# Revit family: Guide_Rail_System-Zoeller-(Z-Rail_Assembly)
name_source: partatom
category: Mechanical Equipment
revit_build: Autodesk Revit 2014 (Build: 20130308_1515(x64)
units: mm (PartAtom-declared; Revit-internal decimal feet)

## types (20) — shared parameters
Assembly Code = D2030400
Bracket Height = 60"
CW Connection = Yes
Default Elevation = 60"
Description = Z-Rail Assembly
HW Connection = No
Height = 60"
Length = 8 1/2"
Manufacturer = Zoeller
Price = Prices may vary. Please consult Manufacturer Representative for most up-to-date price list.
Product Documentation Link = https://www.zoellerpumps.com
Product Page URL = https://www.zoellerpumps.com
Revised Date = 04/10/2019
URL = http://www.zoellerpumps.com
Vent Connection = No
Waste Connection = Yes
Width = 6 3/4"

## per-type parameters (varying)
| type | Carrier Void Diameter 1 | Carrier Void Diameter 2 | Carrier Void Diameter 3 | Elbow Outer Diameter | Material | Model | Non-Sparking Brass | Pump Discharge Diameter | Pump Discharge Radius | Rail Discharge Outer Diameter | Rail Plate Material | Rail System Discharge Diameter | Rail System Discharge Radius | Upper Rail Support Bracket |
| 39-0134 1-1/4" Z-Rail | 1 17/32" | 1 25/32" | 1 31/32" | 1 3/4" | Metal-Zoeller-Epoxy Powder Coated Ductile Iron | 39-0134 | No | 1 1/4" | 5/8" | 2 3/8" | Metal-Zoeller-Powder Coated Ductile Iron | 2" | 1" | Support_Bracket-Upper-Zoeller-Rail_Sytem-152383 : 15-2383 |
| 39-0131 1-1/2" Z-Rail | 1 17/32" | 1 25/32" | 1 31/32" | 2" | Metal-Zoeller-Epoxy Powder Coated Ductile Iron | 39-0131 | No | 1 1/2" | 3/4" | 2 3/8" | Metal-Zoeller-Powder Coated Ductile Iron | 2" | 1" | Support_Bracket-Upper-Zoeller-Rail_Sytem-152383 : 15-2383 |
| 39-0128 2" Z-Rail | 2 1/32" | 2 9/32" | 2 15/32" | 2 1/2" | Metal-Zoeller-Epoxy Powder Coated Ductile Iron | 39-0128 | No | 2" | 1" | 2 3/8" | Metal-Zoeller-Powder Coated Ductile Iron | 2" | 1" | Support_Bracket-Upper-Zoeller-Rail_Sytem-152383 : 15-2383 |
| 39-0135 1-1/4" Z-Rail | 1 17/32" | 1 25/32" | 1 31/32" | 1 3/4" | Metal-Zoeller-Epoxy Powder Coated Ductile Iron | 39-0135 | No | 1 1/4" | 5/8" | 2 3/8" | Metal-Zoeller-Powder Coated Ductile Iron | 2" | 1" | Support_Bracket-Upper-Zoeller-Rail_Sytem-152383 : 15-2383 SS |
| 39-0136 1-1/4" Z-Rail | 1 17/32" | 1 25/32" | 1 31/32" | 1 3/4" | Metal-Zoeller-Powder Coated Ductile Iron | 39-0136 | Yes | 1 1/4" | 5/8" | 2 3/8" | Metal-Zoeller-Bronze | 2" | 1" | Support_Bracket-Upper-Zoeller-Rail_Sytem-152383 : 15-2383 |
| 39-0143 1-1/4" Z-Rail | 1 17/32" | 1 25/32" | 1 31/32" | 1 3/4" | Metal-Zoeller-Powder Coated Ductile Iron | 39-0143 | Yes | 1 1/4" | 5/8" | 2 3/8" | Metal-Zoeller-Bronze | 2" | 1" | Support_Bracket-Upper-Zoeller-Rail_Sytem-152383 : 15-2383 SS |
| 39-0132 1-1/2" Z-Rail | 1 17/32" | 1 25/32" | 1 31/32" | 2" | Metal-Zoeller-Epoxy Powder Coated Ductile Iron | 39-0132 | No | 1 1/2" | 3/4" | 2 3/8" | Metal-Zoeller-Powder Coated Ductile Iron | 2" | 1" | Support_Bracket-Upper-Zoeller-Rail_Sytem-152383 : 15-2383 SS |
| 39-0133 1-1/2" Z-Rail | 1 17/32" | 1 25/32" | 1 31/32" | 2" | Metal-Zoeller-Powder Coated Ductile Iron | 39-0133 | Yes | 1 1/2" | 3/4" | 2 3/8" | Metal-Zoeller-Bronze | 2" | 1" | Support_Bracket-Upper-Zoeller-Rail_Sytem-152383 : 15-2383 |
| 39-0142 1-1/2" Z-Rail | 1 17/32" | 1 25/32" | 1 31/32" | 2" | Metal-Zoeller-Powder Coated Ductile Iron | 39-0142 | Yes | 1 1/2" | 3/4" | 2 3/8" | Metal-Zoeller-Bronze | 2" | 1" | Support_Bracket-Upper-Zoeller-Rail_Sytem-152383 : 15-2383 SS |
| 39-0129 2" Z-Rail | 2 1/32" | 2 9/32" | 2 15/32" | 2 1/2" | Metal-Zoeller-Epoxy Powder Coated Ductile Iron | 39-0129 | No | 2" | 1" | 2 3/8" | Metal-Zoeller-Powder Coated Ductile Iron | 2" | 1" | Support_Bracket-Upper-Zoeller-Rail_Sytem-152383 : 15-2383 SS |
| 39-0130 2" Z-Rail | 2 1/32" | 2 9/32" | 2 15/32" | 2 1/2" | Metal-Zoeller-Powder Coated Ductile Iron | 39-0130 | Yes | 2" | 1" | 2 3/8" | Metal-Zoeller-Bronze | 2" | 1" | Support_Bracket-Upper-Zoeller-Rail_Sytem-152383 : 15-2383 |
| 39-0141 2" Z-Rail | 2 1/32" | 2 9/32" | 2 15/32" | 2 1/2" | Metal-Zoeller-Powder Coated Ductile Iron | 39-0141 | Yes | 2" | 1" | 2 3/8" | Metal-Zoeller-Bronze | 2" | 1" | Support_Bracket-Upper-Zoeller-Rail_Sytem-152383 : 15-2383 SS |
| 39-0146 2" Z-Rail | 2 1/32" | 2 9/32" | 2 15/32" | 2 1/2" | Metal-Zoeller-Powder Coated Ductile Iron | 39-0146 | No | 2" | 1" | 2 3/8" | Metal-Zoeller-Powder Coated Ductile Iron | 2" | 1" | Support_Bracket-Upper-Zoeller-Rail_Sytem-152383 : 15-2383 |
| 39-0148 2" Z-Rail | 2 1/32" | 2 9/32" | 2 15/32" | 2 1/2" | Metal-Zoeller-Powder Coated Ductile Iron | 39-0148 | No | 2" | 1" | 2 3/8" | Metal-Zoeller-Powder Coated Ductile Iron | 2" | 1" | Support_Bracket-Upper-Zoeller-Rail_Sytem-152383 : 15-2383 SS |
| 39-0147 2" Z-Rail | 2 1/32" | 2 9/32" | 2 15/32" | 2 1/2" | Metal-Zoeller-Powder Coated Ductile Iron | 39-0147 | Yes | 2" | 1" | 2 3/8" | Metal-Zoeller-Bronze | 2" | 1" | Support_Bracket-Upper-Zoeller-Rail_Sytem-152383 : 15-2383 |
| 39-0149 2" Z-Rail | 2 1/32" | 2 9/32" | 2 15/32" | 2 1/2" | Metal-Zoeller-Powder Coated Ductile Iron | 39-0149 | Yes | 2" | 1" | 2 3/8" | Metal-Zoeller-Bronze | 2" | 1" | Support_Bracket-Upper-Zoeller-Rail_Sytem-152383 : 15-2383 SS |
| 39-0122 3" Z-Rail | 1 17/32" | 1 25/32" | 1 31/32" | 3 1/2" | Metal-Zoeller-Epoxy Powder Coated Ductile Iron | 39-0122 | No | 3" | 1 1/2" | 3 3/8" | Metal-Zoeller-Powder Coated Ductile Iron | 3" | 1 1/2" | Support_Bracket-Upper-Zoeller-Rail_Sytem-152383 : 15-2383 |
| 39-0123 3" Z-Rail | 1 17/32" | 1 25/32" | 1 31/32" | 3 1/2" | Metal-Zoeller-Epoxy Powder Coated Ductile Iron | 39-0123 | No | 3" | 1 1/2" | 3 3/8" | Metal-Zoeller-Powder Coated Ductile Iron | 3" | 1 1/2" | Support_Bracket-Upper-Zoeller-Rail_Sytem-152383 : 15-2383 SS |
| 39-0124 3" Z-Rail | 1 17/32" | 1 25/32" | 1 31/32" | 3 1/2" | Metal-Zoeller-Powder Coated Ductile Iron | 39-0124 | Yes | 3" | 1 1/2" | 3 3/8" | Metal-Zoeller-Bronze | 3" | 1 1/2" | Support_Bracket-Upper-Zoeller-Rail_Sytem-152383 : 15-2383 |
| 39-0125 3" Z-Rail | 1 17/32" | 1 25/32" | 1 31/32" | 3 1/2" | Metal-Zoeller-Powder Coated Ductile Iron | 39-0125 | Yes | 3" | 1 1/2" | 3 3/8" | Metal-Zoeller-Bronze | 3" | 1 1/2" | Support_Bracket-Upper-Zoeller-Rail_Sytem-152383 : 15-2383 SS |

## geometry (parser evidence)
native form markers: Sweep x4
no freeform markers — native parametric forms only
